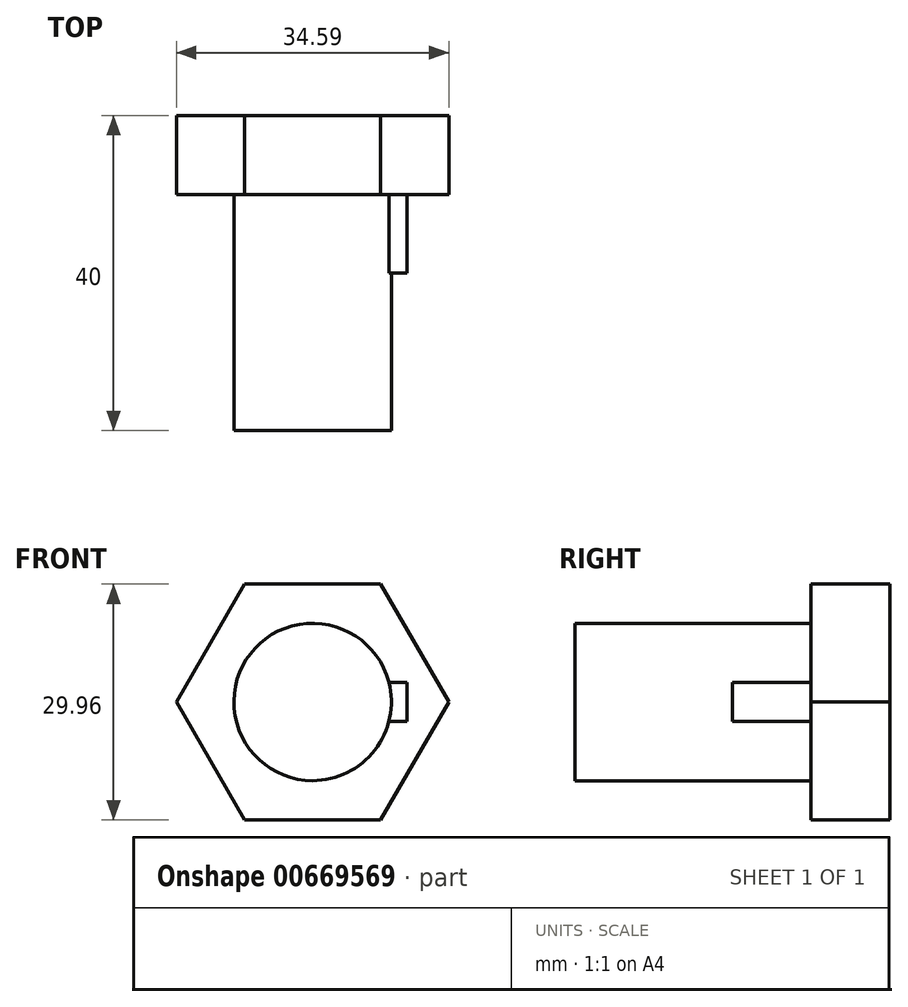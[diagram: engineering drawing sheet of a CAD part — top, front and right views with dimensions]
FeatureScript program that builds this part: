
annotation { "Feature Type Name" : "Feature", "Feature Type Description" : "" }
export const myFeature = defineFeature(function(context is Context, id is Id, definition is map)
    precondition{}
    {
        {
            var Q0;
            Q0=qCreatedBy(makeId("Front.planeOp"),FACE);
            var sketch = newSketch(context, id + "F0", { "sketchPlane" : qUnion([Q0])});
            skCircle(sketch, "E0.cCircle", {"center": v(-165.47, 0) * mm, "radius": 14.98 * mm, "construction": true});
            skLineSegment(sketch, "E0.0", {"start": v(-156.82, -14.98) * mm, "end": v(-174.11, -14.98) * mm});
            skLineSegment(sketch, "E0.1", {"start": v(-174.11, -14.98) * mm, "end": v(-182.76, 0) * mm});
            skLineSegment(sketch, "E0.2", {"start": v(-182.76, 0) * mm, "end": v(-174.11, 14.98) * mm});
            skLineSegment(sketch, "E0.3", {"start": v(-174.11, 14.98) * mm, "end": v(-156.82, 14.98) * mm});
            skLineSegment(sketch, "E0.4", {"start": v(-156.82, 14.98) * mm, "end": v(-148.17, 0) * mm});
            skLineSegment(sketch, "E0.5", {"start": v(-148.17, 0) * mm, "end": v(-156.82, -14.98) * mm});
            skPoint(sketch, "E0.0.midPoint", {"position": v(-165.47, -14.98) * mm});
            skCircle(sketch, "E1", {"center": v(-165.47, 0) * mm, "radius": 10 * mm});
            skLineSegment(sketch, "E2.bottom", {"start": v(-153.47, -2.5) * mm, "end": v(-155.78, -2.5) * mm});
            skLineSegment(sketch, "E2.top", {"start": v(-153.47, 2.5) * mm, "end": v(-155.78, 2.5) * mm});
            skLineSegment(sketch, "E2.left", {"start": v(-153.47, -2.5) * mm, "end": v(-153.47, 2.5) * mm});
            skPoint(sketch, "E2.middle", {"position": v(-155.47, 0) * mm});
            skPoint(sketch, "E3.orphan", {"position": v(-157.47, 2.5) * mm});
            skPoint(sketch, "E4.orphan", {"position": v(-157.47, -2.5) * mm});
            skSolve(sketch);
        }
        {
            var Q0;
            {var subQ0=sQuery(id+"F0.wireOp",EDGE,"E1");var subQ1=makeQuery(id+"F0.imprint","INTERSECT",VERTEX,{"derivedFrom":[subQ0,sQuery(id+"F0.wireOp",EDGE,"E2.bottom")]});Q0=makeQuery(id+"F0.imprint","IMPRINT",FACE,{"disambiguationData":[TD([[makeQuery(id+"F0.imprint","IMPRINT",EDGE,{"disambiguationData":[TD([[subQ1,1.0]])],"derivedFrom":subQ0}),1.0]])]});}
            extrude(context, id + "F1", {"entities" : qUnion([Q0]), "depth" : 30 * mm, "offsetDistance" : 25 * mm});
        }
        {
            var Q0;
            {var subQ0=sQuery(id+"F0.wireOp",EDGE,"E2.bottom");Q0=makeQuery(id+"F0.imprint","IMPRINT",FACE,{"disambiguationData":[TD([[makeQuery(id+"F0.imprint","IMPRINT",EDGE,{"derivedFrom":subQ0}),-1.0]])]});}
            extrude(context, id + "F2", {"entities" : qUnion([Q0]), "operationType" : NewBodyOperationType.ADD, "depth" : 10 * mm, "offsetDistance" : 25 * mm});
        }
        {
            var Q0;
            Q0=makeQuery(id+"F0.imprint","IMPRINT",FACE,{"disambiguationData":[TD([[makeQuery(id+"F0.imprint","IMPRINT",EDGE,{"derivedFrom":sQuery(id+"F0.wireOp",EDGE,"E0.0")}),-1.0]])]});
            var Q1;
            {var subQ0=sQuery(id+"F0.wireOp",EDGE,"E1");var subQ1=makeQuery(id+"F0.imprint","INTERSECT",VERTEX,{"derivedFrom":[subQ0,sQuery(id+"F0.wireOp",EDGE,"E2.bottom")]});Q1=makeQuery(id+"F0.imprint","IMPRINT",FACE,{"disambiguationData":[TD([[makeQuery(id+"F0.imprint","IMPRINT",EDGE,{"disambiguationData":[TD([[subQ1,1.0]])],"derivedFrom":subQ0}),1.0]])]});}
            var Q2;
            {var subQ0=sQuery(id+"F0.wireOp",EDGE,"E2.bottom");Q2=makeQuery(id+"F0.imprint","IMPRINT",FACE,{"disambiguationData":[TD([[makeQuery(id+"F0.imprint","IMPRINT",EDGE,{"derivedFrom":subQ0}),-1.0]])]});}
            extrude(context, id + "F3", {"entities" : qUnion([Q0, Q1, Q2]), "operationType" : NewBodyOperationType.ADD, "oppositeDirection" : true, "depth" : 10 * mm, "offsetDistance" : 25 * mm});
        }
    });
